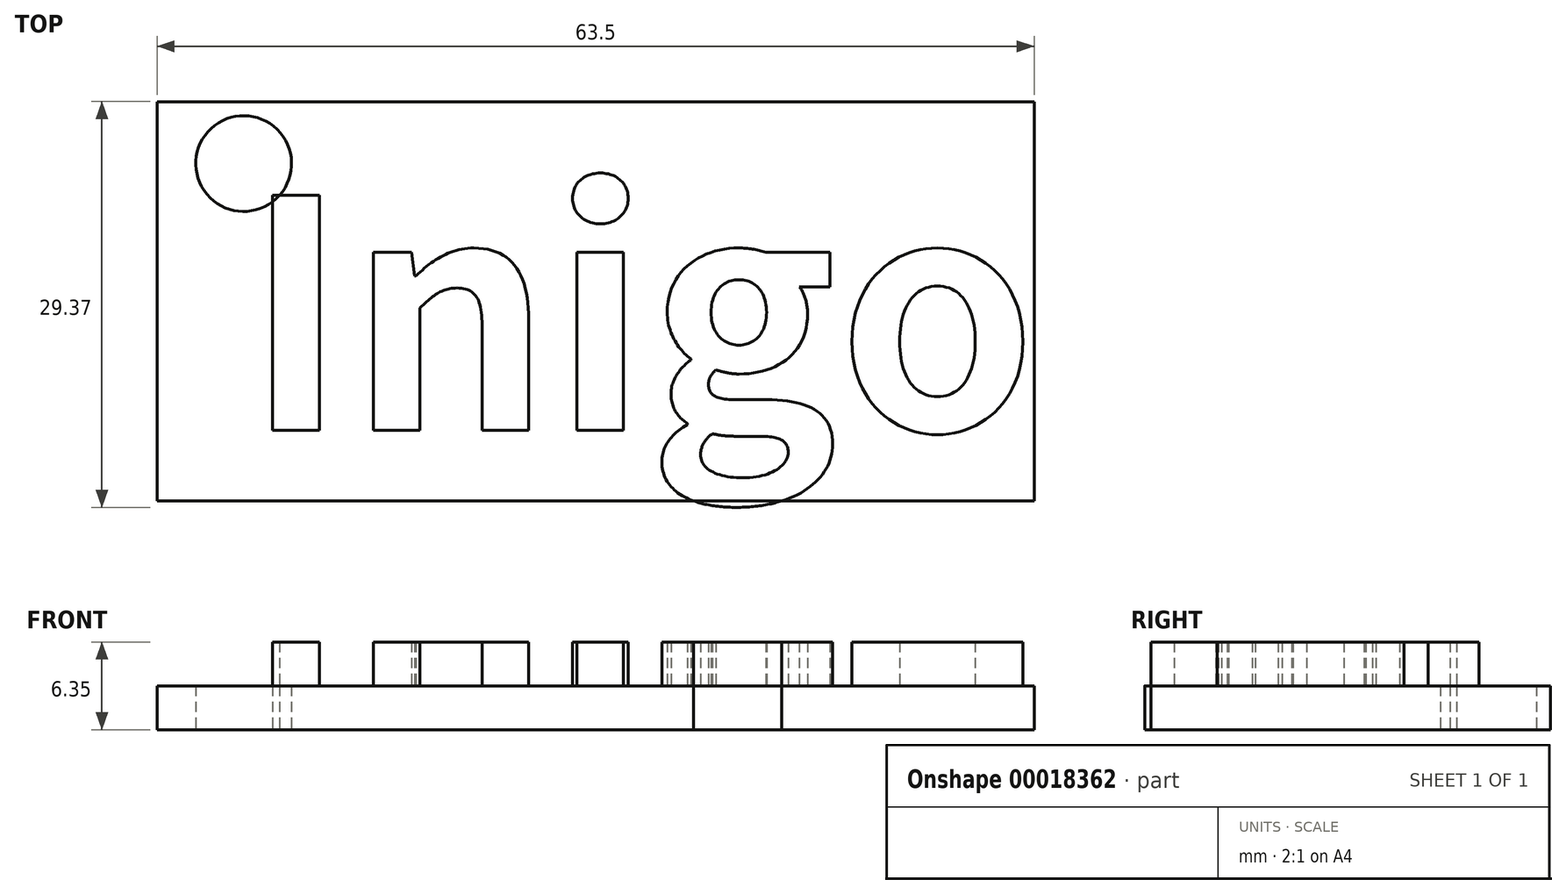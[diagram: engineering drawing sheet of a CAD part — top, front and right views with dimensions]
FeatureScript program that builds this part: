
annotation { "Feature Type Name" : "Feature", "Feature Type Description" : "" }
export const myFeature = defineFeature(function(context is Context, id is Id, definition is map)
    precondition{}
    {
        {
            var Q0;
            Q0=qCreatedBy(makeId("Top.planeOp"),FACE);
            var sketch = newSketch(context, id + "F0", { "sketchPlane" : qUnion([Q0])});
            skLineSegment(sketch, "E0", {"start": v(0, 28.9) * mm, "end": v(0, 0) * mm});
            skLineSegment(sketch, "E1", {"start": v(0, 0) * mm, "end": v(63.5, 0) * mm});
            skLineSegment(sketch, "E2", {"start": v(63.5, 0) * mm, "end": v(63.5, 28.9) * mm});
            skLineSegment(sketch, "E3", {"start": v(63.5, 28.9) * mm, "end": v(0, 28.9) * mm});
            skText(sketch, "E4", { "text": "Inigo", "fontName": "NotoSansCJKkr-Bold.otf"});
            skCircle(sketch, "E5", {"center": v(6.27, 24.43) * mm, "radius": 3.47 * mm});
            const initialGuessF0  = {"E4": [0.00627, 0.00512, 1, 0, 0.01655]};
            skSetInitialGuess(sketch, initialGuessF0);
            skSolve(sketch);
        }
        {
            var Q0;
            Q0 = qSketchRegion(id + "F0", true);
            var Q1;
            {var subQ11=sQuery(id+"F0.wireOp",EDGE,"E0");Q1=makeQuery(id+"F0.imprint","IMPRINT",FACE,{"disambiguationData":[TD([[makeQuery(id+"F0.imprint","IMPRINT",EDGE,{"derivedFrom":subQ11}),1.0]])]});}
            var Q2;
            {var subQ5=sQuery(id+"F0.wireOp",EDGE,"E4.sketch_text.stroke-26");Q2=makeQuery(id+"F0.imprint","IMPRINT",FACE,{"disambiguationData":[TD([[makeQuery(id+"F0.imprint","IMPRINT",EDGE,{"derivedFrom":subQ5}),1.0]])]});}
            var Q3;
            Q3=makeQuery(id+"F0.imprint","IMPRINT",FACE,{"disambiguationData":[TD([[makeQuery(id+"F0.imprint","IMPRINT",EDGE,{"derivedFrom":sQuery(id+"F0.wireOp",EDGE,"E4.sketch_text.stroke-55")}),1.0]])]});
            var Q4;
            {var subQ5=sQuery(id+"F0.wireOp",EDGE,"E4.sketch_text.stroke-0");Q4=makeQuery(id+"F0.imprint","IMPRINT",FACE,{"disambiguationData":[TD([[makeQuery(id+"F0.imprint","IMPRINT",EDGE,{"derivedFrom":subQ5}),1.0]])]});}
            var Q5;
            Q5=makeQuery(id+"F0.imprint","IMPRINT",FACE,{"disambiguationData":[TD([[makeQuery(id+"F0.imprint","IMPRINT",EDGE,{"derivedFrom":sQuery(id+"F0.wireOp",EDGE,"E4.sketch_text.stroke-59")}),-1.0]])]});
            var Q6;
            Q6=makeQuery(id+"F0.imprint","IMPRINT",FACE,{"disambiguationData":[TD([[makeQuery(id+"F0.imprint","IMPRINT",EDGE,{"derivedFrom":sQuery(id+"F0.wireOp",EDGE,"E4.sketch_text.stroke-49")}),-1.0]])]});
            var Q7;
            Q7=makeQuery(id+"F0.imprint","IMPRINT",FACE,{"disambiguationData":[TD([[makeQuery(id+"F0.imprint","IMPRINT",EDGE,{"derivedFrom":sQuery(id+"F0.wireOp",EDGE,"E4.sketch_text.stroke-45")}),-1.0]])]});
            var Q8;
            Q8=makeQuery(id+"F0.imprint","IMPRINT",FACE,{"disambiguationData":[TD([[makeQuery(id+"F0.imprint","IMPRINT",EDGE,{"derivedFrom":sQuery(id+"F0.wireOp",EDGE,"E4.sketch_text.stroke-21")}),1.0]])]});
            var Q9;
            Q9=makeQuery(id+"F0.imprint","IMPRINT",FACE,{"disambiguationData":[TD([[makeQuery(id+"F0.imprint","IMPRINT",EDGE,{"derivedFrom":sQuery(id+"F0.wireOp",EDGE,"E4.sketch_text.stroke-17")}),1.0]])]});
            var Q10;
            Q10=makeQuery(id+"F0.imprint","IMPRINT",FACE,{"disambiguationData":[TD([[makeQuery(id+"F0.imprint","IMPRINT",EDGE,{"derivedFrom":sQuery(id+"F0.wireOp",EDGE,"E4.sketch_text.stroke-4")}),1.0]])]});
            var Q11;
            {var subQ1=sQuery(id+"F0.wireOp",EDGE,"E4.sketch_text.stroke-3");var subQ3=sQuery(id+"F0.wireOp",EDGE,"E4.sketch_text.stroke-2");var subQ5=makeQuery(id+"F0.imprint","INTERSECT",VERTEX,{"derivedFrom":[subQ3,subQ1]});Q11=makeQuery(id+"F0.imprint","IMPRINT",FACE,{"disambiguationData":[TD([[makeQuery(id+"F0.imprint","IMPRINT",EDGE,{"disambiguationData":[TD([[subQ5,1.0]])],"derivedFrom":subQ3}),1.0]])]});}
            var Q12;
            {var subQ0=sQuery(id+"F0.wireOp",EDGE,"E4.sketch_text.stroke-44");var subQ1=sQuery(id+"F0.wireOp",EDGE,"E1");var subQ2=makeQuery(id+"F0.imprint","INTERSECT",VERTEX,{"derivedFrom":[subQ1,subQ0]});Q12=makeQuery(id+"F0.imprint","IMPRINT",FACE,{"disambiguationData":[TD([[makeQuery(id+"F0.imprint","IMPRINT",EDGE,{"disambiguationData":[TD([[subQ2,-1.0]])],"derivedFrom":subQ1}),-1.0]])]});}
            extrude(context, id + "F1", {"entities" : qUnion([Q0, Q1, Q2, Q3, Q4, Q5, Q6, Q7, Q8, Q9, Q10, Q11, Q12]), "depth" : 3.17 * mm});
        }
        {
            var Q0;
            {var subQ5=sQuery(id+"F0.wireOp",EDGE,"E4.sketch_text.stroke-0");Q0=makeQuery(id+"F0.imprint","IMPRINT",FACE,{"disambiguationData":[TD([[makeQuery(id+"F0.imprint","IMPRINT",EDGE,{"derivedFrom":subQ5}),1.0]])]});}
            var Q1;
            Q1=makeQuery(id+"F0.imprint","IMPRINT",FACE,{"disambiguationData":[TD([[makeQuery(id+"F0.imprint","IMPRINT",EDGE,{"derivedFrom":sQuery(id+"F0.wireOp",EDGE,"E4.sketch_text.stroke-4")}),1.0]])]});
            var Q2;
            Q2=makeQuery(id+"F0.imprint","IMPRINT",FACE,{"disambiguationData":[TD([[makeQuery(id+"F0.imprint","IMPRINT",EDGE,{"derivedFrom":sQuery(id+"F0.wireOp",EDGE,"E4.sketch_text.stroke-17")}),1.0]])]});
            var Q3;
            Q3=makeQuery(id+"F0.imprint","IMPRINT",FACE,{"disambiguationData":[TD([[makeQuery(id+"F0.imprint","IMPRINT",EDGE,{"derivedFrom":sQuery(id+"F0.wireOp",EDGE,"E4.sketch_text.stroke-21")}),1.0]])]});
            var Q4;
            {var subQ5=sQuery(id+"F0.wireOp",EDGE,"E4.sketch_text.stroke-26");Q4=makeQuery(id+"F0.imprint","IMPRINT",FACE,{"disambiguationData":[TD([[makeQuery(id+"F0.imprint","IMPRINT",EDGE,{"derivedFrom":subQ5}),1.0]])]});}
            var Q5;
            Q5=makeQuery(id+"F0.imprint","IMPRINT",FACE,{"disambiguationData":[TD([[makeQuery(id+"F0.imprint","IMPRINT",EDGE,{"derivedFrom":sQuery(id+"F0.wireOp",EDGE,"E4.sketch_text.stroke-55")}),1.0]])]});
            extrude(context, id + "F2", {"entities" : qUnion([Q0, Q1, Q2, Q3, Q4, Q5]), "operationType" : NewBodyOperationType.ADD, "depth" : 6.35 * mm});
        }
    });
